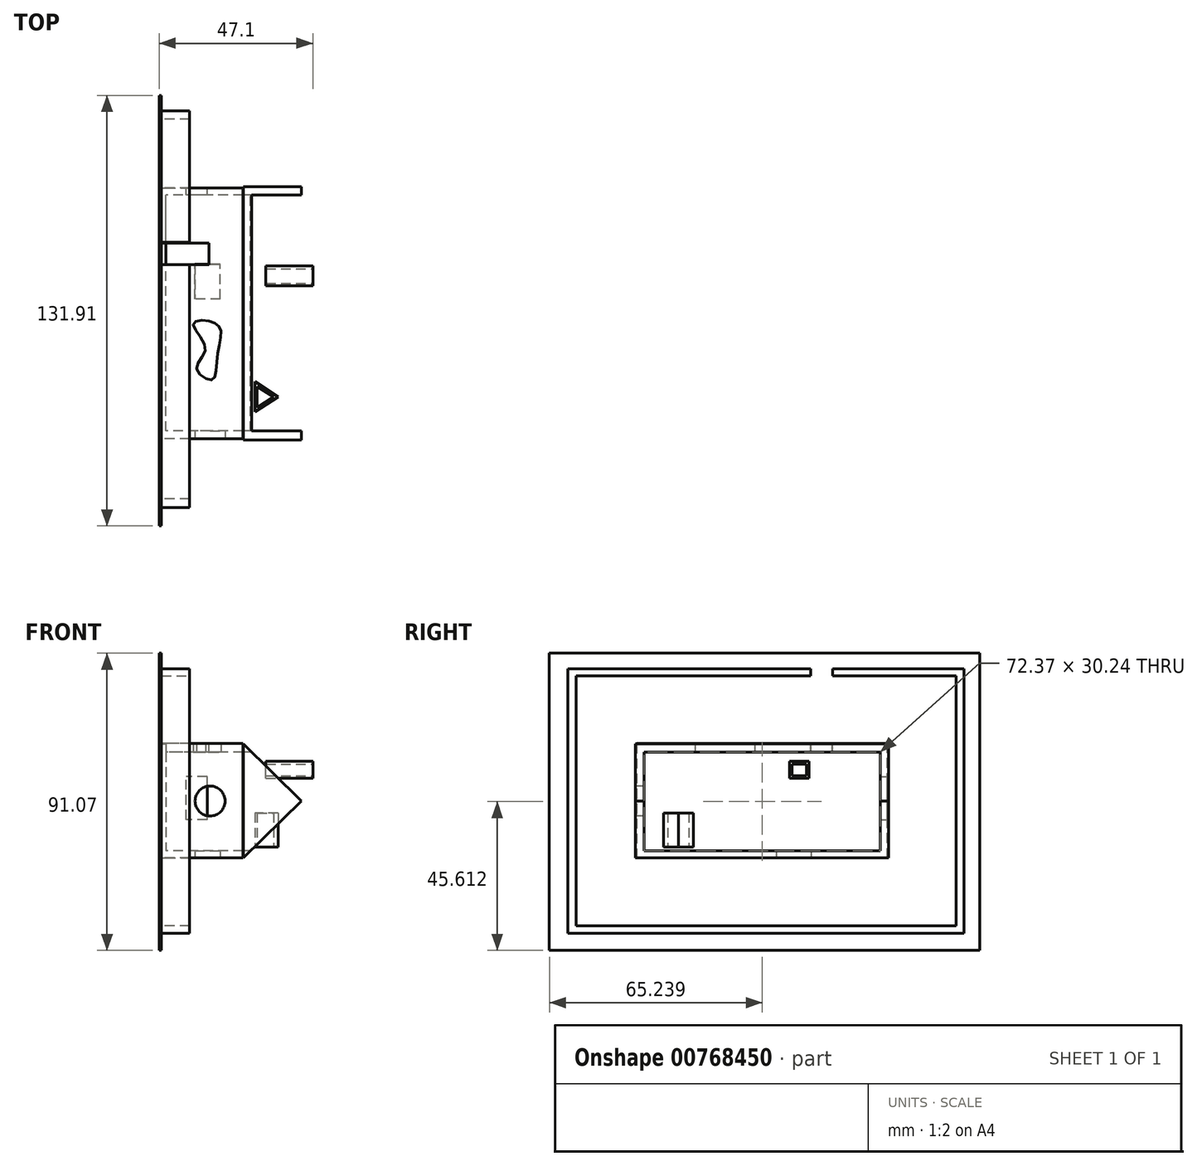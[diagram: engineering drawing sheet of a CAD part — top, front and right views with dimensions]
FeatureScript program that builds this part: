
annotation { "Feature Type Name" : "Feature", "Feature Type Description" : "" }
export const myFeature = defineFeature(function(context is Context, id is Id, definition is map)
    precondition{}
    {
        {
            var Q0;
            Q0=qCreatedBy(makeId("Right.planeOp"),FACE);
            var sketch = newSketch(context, id + "F0", { "sketchPlane" : qUnion([Q0])});
            skLineSegment(sketch, "E0.bottom", {"start": v(-30.7, 35.03) * mm, "end": v(46.12, 35.03) * mm});
            skLineSegment(sketch, "E0.top", {"start": v(-30.7, 0) * mm, "end": v(46.12, 0) * mm});
            skLineSegment(sketch, "E0.left", {"start": v(-30.7, 35.03) * mm, "end": v(-30.7, 0) * mm});
            skLineSegment(sketch, "E0.right", {"start": v(46.12, 35.03) * mm, "end": v(46.12, 0) * mm});
            skSolve(sketch);
        }
        {
            var Q0;
            Q0=makeQuery(id+"F0.imprint","IMPRINT",FACE,{"disambiguationData":[TD([[makeQuery(id+"F0.imprint","IMPRINT",EDGE,{"derivedFrom":sQuery(id+"F0.wireOp",EDGE,"E0.bottom")}),-1.0]])]});
            extrude(context, id + "F1", {"entities" : qUnion([Q0]), "depth" : 25 * mm, "offsetDistance" : 25 * mm});
        }
        {
            var Q0;
            Q0=makeQuery(id+"F1.opExtrude","SWEPT_FACE",FACE,{"disambiguationData":[OSD([sQuery(id+"F0.wireOp",EDGE,"E0.left")])]});
            cPlane(context, id + "F2", {"entities" : qUnion([Q0]), "cplaneType" : CPlaneType.OFFSET, "offset" : 0.4 * mm, "width" : 150 * mm, "height" : 150 * mm});
        }
        {
            var Q0;
            Q0=qCreatedBy(id+"F2.planeOp",FACE);
            var sketch = newSketch(context, id + "F3", { "sketchPlane" : qUnion([Q0])});
            skLineSegment(sketch, "E1", {"start": v(25.09, 0) * mm, "end": v(25.09, 34.92) * mm});
            skLineSegment(sketch, "E2", {"start": v(25.09, 34.92) * mm, "end": v(42.88, 17.46) * mm});
            skLineSegment(sketch, "E3", {"start": v(42.88, 17.46) * mm, "end": v(25.09, 0) * mm});
            skPoint(sketch, "E4", {"position": v(25.09, 17.46) * mm});
            skSolve(sketch);
        }
        {
            var Q0;
            Q0=makeQuery(id+"F3.imprint","IMPRINT",FACE,{"disambiguationData":[TD([[makeQuery(id+"F3.imprint","IMPRINT",EDGE,{"derivedFrom":sQuery(id+"F3.wireOp",EDGE,"E1")}),-1.0]])]});
            extrude(context, id + "F4", {"entities" : qUnion([Q0]), "oppositeDirection" : true, "depth" : 77.6 * mm, "offsetDistance" : 25 * mm});
        }
        {
            var Q0;
            Q0=makeQuery(id+"F1.opExtrude","CAP_FACE",FACE,{"disambiguationData":[OSD([sQuery(id+"F0.wireOp",EDGE,"E0.bottom"),sQuery(id+"F0.wireOp",EDGE,"E0.top"),sQuery(id+"F0.wireOp",EDGE,"E0.left"),sQuery(id+"F0.wireOp",EDGE,"E0.right")])],"isStart":true});
            var sketch = newSketch(context, id + "F5", { "sketchPlane" : qUnion([Q0])});
            skLineSegment(sketch, "E5.bottom", {"start": v(28.4, 32.4) * mm, "end": v(-43.98, 32.4) * mm});
            skLineSegment(sketch, "E5.top", {"start": v(28.4, 2.15) * mm, "end": v(-43.98, 2.15) * mm});
            skLineSegment(sketch, "E5.left", {"start": v(28.4, 32.4) * mm, "end": v(28.4, 2.15) * mm});
            skLineSegment(sketch, "E5.right", {"start": v(-43.98, 32.4) * mm, "end": v(-43.98, 2.15) * mm});
            skLineSegment(sketch, "E6.bottom", {"start": v(-43.98, 12.73) * mm, "end": v(-46.12, 12.73) * mm});
            skLineSegment(sketch, "E6.top", {"start": v(-43.98, 20.43) * mm, "end": v(-46.12, 20.43) * mm});
            skLineSegment(sketch, "E6.left", {"start": v(-43.98, 12.73) * mm, "end": v(-43.98, 20.43) * mm});
            skLineSegment(sketch, "E6.right", {"start": v(-46.12, 12.73) * mm, "end": v(-46.12, 20.43) * mm});
            skSolve(sketch);
        }
        {
            var Q0;
            Q0=makeQuery(id+"F5.imprint","IMPRINT",FACE,{"disambiguationData":[TD([[makeQuery(id+"F5.imprint","IMPRINT",EDGE,{"derivedFrom":sQuery(id+"F5.wireOp",EDGE,"E5.bottom")}),1.0]])]});
            extrude(context, id + "F6", {"entities" : qUnion([Q0]), "operationType" : NewBodyOperationType.REMOVE, "oppositeDirection" : true, "depth" : 113 * mm, "offsetDistance" : 25 * mm});
        }
        {
            var Q0;
            Q0=makeQuery(id+"F1.opExtrude","SWEPT_FACE",FACE,{"disambiguationData":[OSD([sQuery(id+"F0.wireOp",EDGE,"E0.top")])]});
            var sketch = newSketch(context, id + "F7", { "sketchPlane" : qUnion([Q0])});
            skLineSegment(sketch, "E7.bottom", {"start": v(18.02, -12.07) * mm, "end": v(10.18, -12.07) * mm});
            skLineSegment(sketch, "E7.top", {"start": v(18.02, -22.75) * mm, "end": v(10.18, -22.75) * mm});
            skLineSegment(sketch, "E7.left", {"start": v(18.02, -12.07) * mm, "end": v(18.02, -22.75) * mm});
            skLineSegment(sketch, "E7.right", {"start": v(10.18, -12.07) * mm, "end": v(10.18, -22.75) * mm});
            skSolve(sketch);
        }
        {
            var Q0;
            Q0=makeQuery(id+"F7.imprint","IMPRINT",FACE,{"disambiguationData":[TD([[makeQuery(id+"F7.imprint","IMPRINT",EDGE,{"derivedFrom":sQuery(id+"F7.wireOp",EDGE,"E7.bottom")}),1.0]])]});
            extrude(context, id + "F8", {"entities" : qUnion([Q0]), "operationType" : NewBodyOperationType.REMOVE, "oppositeDirection" : true, "depth" : 25 * mm, "offsetDistance" : 25 * mm});
        }
        {
            var Q0;
            Q0=makeQuery(id+"F1.opExtrude","SWEPT_FACE",FACE,{"disambiguationData":[OSD([sQuery(id+"F0.wireOp",EDGE,"E0.bottom")])]});
            var sketch = newSketch(context, id + "F9", { "sketchPlane" : qUnion([Q0])});
            skLineSegment(sketch, "E8.bottom", {"start": v(14.58, 29.22) * mm, "end": v(0, 29.22) * mm});
            skLineSegment(sketch, "E8.top", {"start": v(14.58, 22.6) * mm, "end": v(0, 22.6) * mm});
            skLineSegment(sketch, "E8.left", {"start": v(14.58, 29.22) * mm, "end": v(14.58, 22.6) * mm});
            skLineSegment(sketch, "E8.right", {"start": v(0, 29.22) * mm, "end": v(0, 22.6) * mm});
            skSolve(sketch);
        }
        {
            var Q0;
            Q0=makeQuery(id+"F9.imprint","IMPRINT",FACE,{"disambiguationData":[TD([[makeQuery(id+"F9.imprint","IMPRINT",EDGE,{"derivedFrom":sQuery(id+"F9.wireOp",EDGE,"E8.bottom")}),1.0]])]});
            extrude(context, id + "F10", {"entities" : qUnion([Q0]), "operationType" : NewBodyOperationType.REMOVE, "oppositeDirection" : true, "depth" : 25 * mm, "offsetDistance" : 25 * mm});
        }
        {
            var Q0;
            Q0=makeQuery(id+"F1.opExtrude","SWEPT_FACE",FACE,{"disambiguationData":[OSD([sQuery(id+"F0.wireOp",EDGE,"E0.left")])]});
            var sketch = newSketch(context, id + "F11", { "sketchPlane" : qUnion([Q0])});
            skCircle(sketch, "E9", {"center": v(14.88, 17.43) * mm, "radius": 4.6 * mm});
            skSolve(sketch);
        }
        {
            var Q0;
            Q0=makeQuery(id+"F11.imprint","IMPRINT",FACE,{"disambiguationData":[TD([[makeQuery(id+"F11.imprint","IMPRINT",EDGE,{"derivedFrom":sQuery(id+"F11.wireOp",EDGE,"E9")}),1.0]])]});
            extrude(context, id + "F12", {"entities" : qUnion([Q0]), "operationType" : NewBodyOperationType.REMOVE, "oppositeDirection" : true, "depth" : 25 * mm, "offsetDistance" : 25 * mm});
        }
        {
            var Q0;
            Q0=makeQuery(id+"F1.opExtrude","SWEPT_FACE",FACE,{"disambiguationData":[OSD([sQuery(id+"F0.wireOp",EDGE,"E0.bottom")])]});
            var sketch = newSketch(context, id + "F13", { "sketchPlane" : qUnion([Q0])});
            skFitSpline(sketch, "E10", {"points": [v(14.56, 5.34) * mm, v(18.11, 2.68) * mm, v(17.03, -6.13) * mm, v(15.45, -12.74) * mm, v(10.78, -9.13) * mm, v(13.5, -3.04) * mm, v(9.73, 4.4) * mm, v(14.56, 5.34) * mm]});
            skSolve(sketch);
        }
        {
            var Q0;
            Q0=makeQuery(id+"F13.imprint","IMPRINT",FACE,{"disambiguationData":[TD([[makeQuery(id+"F13.imprint","IMPRINT",EDGE,{"derivedFrom":sQuery(id+"F13.wireOp",EDGE,"E10")}),-1.0]])]});
            extrude(context, id + "F14", {"entities" : qUnion([Q0]), "operationType" : NewBodyOperationType.REMOVE, "oppositeDirection" : true, "depth" : 25 * mm, "offsetDistance" : 25 * mm});
        }
        {
            var Q0;
            Q0=qCreatedBy(makeId("Right.planeOp"),FACE);
            cPlane(context, id + "F15", {"entities" : qUnion([Q0]), "cplaneType" : CPlaneType.OFFSET, "offset" : 46.4 * mm, "width" : 150 * mm, "height" : 150 * mm});
        }
        {
            var Q0;
            Q0=qCreatedBy(id+"F15.planeOp",FACE);
            var sketch = newSketch(context, id + "F16", { "sketchPlane" : qUnion([Q0])});
            skLineSegment(sketch, "E11.bottom", {"start": v(22.16, 24.47) * mm, "end": v(16.16, 24.47) * mm});
            skLineSegment(sketch, "E11.top", {"start": v(22.16, 29.6) * mm, "end": v(16.16, 29.6) * mm});
            skLineSegment(sketch, "E11.left", {"start": v(22.16, 24.47) * mm, "end": v(22.16, 29.6) * mm});
            skLineSegment(sketch, "E11.right", {"start": v(16.16, 24.47) * mm, "end": v(16.16, 29.6) * mm});
            skSolve(sketch);
        }
        {
            var Q0;
            Q0=makeQuery(id+"F16.imprint","IMPRINT",FACE,{"disambiguationData":[TD([[makeQuery(id+"F16.imprint","IMPRINT",EDGE,{"derivedFrom":sQuery(id+"F16.wireOp",EDGE,"E11.bottom")}),-1.0]])]});
            extrude(context, id + "F17", {"entities" : qUnion([Q0]), "operationType" : NewBodyOperationType.ADD, "oppositeDirection" : true, "depth" : 14.4 * mm, "offsetDistance" : 25 * mm});
        }
        {
            var Q0;
            Q0=makeQuery(id+"F17.opExtrude","CAP_FACE",FACE,{"disambiguationData":[OSD([sQuery(id+"F16.wireOp",EDGE,"E11.bottom"),sQuery(id+"F16.wireOp",EDGE,"E11.top"),sQuery(id+"F16.wireOp",EDGE,"E11.left"),sQuery(id+"F16.wireOp",EDGE,"E11.right")])],"isStart":true});
            var sketch = newSketch(context, id + "F18", { "sketchPlane" : qUnion([Q0])});
            skLineSegment(sketch, "E12.bottom", {"start": v(21.35, 25.23) * mm, "end": v(16.92, 25.23) * mm});
            skLineSegment(sketch, "E12.top", {"start": v(21.35, 28.75) * mm, "end": v(16.92, 28.75) * mm});
            skLineSegment(sketch, "E12.left", {"start": v(21.35, 25.23) * mm, "end": v(21.35, 28.75) * mm});
            skLineSegment(sketch, "E12.right", {"start": v(16.92, 25.23) * mm, "end": v(16.92, 28.75) * mm});
            skSolve(sketch);
        }
        {
            var Q0;
            Q0=makeQuery(id+"F18.imprint","IMPRINT",FACE,{"disambiguationData":[TD([[makeQuery(id+"F18.imprint","IMPRINT",EDGE,{"derivedFrom":sQuery(id+"F18.wireOp",EDGE,"E12.bottom")}),-1.0]])]});
            extrude(context, id + "F19", {"entities" : qUnion([Q0]), "operationType" : NewBodyOperationType.REMOVE, "oppositeDirection" : true, "depth" : 25 * mm, "offsetDistance" : 25 * mm});
        }
        {
            var Q0;
            Q0=qCreatedBy(makeId("Right.planeOp"),FACE);
            var sketch = newSketch(context, id + "F20", { "sketchPlane" : qUnion([Q0])});
            skLineSegment(sketch, "E13.bottom", {"start": v(-30.64, 34.9) * mm, "end": v(46.1, 34.9) * mm});
            skLineSegment(sketch, "E13.top", {"start": v(-30.64, 0) * mm, "end": v(46.1, 0) * mm});
            skLineSegment(sketch, "E13.left", {"start": v(-30.64, 34.9) * mm, "end": v(-30.64, 0) * mm});
            skLineSegment(sketch, "E13.right", {"start": v(46.1, 34.9) * mm, "end": v(46.1, 0) * mm});
            skSolve(sketch);
        }
        {
            var Q0;
            Q0=makeQuery(id+"F20.imprint","IMPRINT",FACE,{"disambiguationData":[TD([[makeQuery(id+"F20.imprint","IMPRINT",EDGE,{"derivedFrom":sQuery(id+"F20.wireOp",EDGE,"E13.bottom")}),-1.0]])]});
            extrude(context, id + "F21", {"entities" : qUnion([Q0]), "operationType" : NewBodyOperationType.ADD, "depth" : 1.3 * mm, "offsetDistance" : 25 * mm});
        }
        {
            var Q0;
            Q0=qCreatedBy(makeId("Right.planeOp"),FACE);
            var sketch = newSketch(context, id + "F22", { "sketchPlane" : qUnion([Q0])});
            skLineSegment(sketch, "E14.bottom", {"start": v(74.46, -28.34) * mm, "end": v(-57.45, -28.34) * mm});
            skLineSegment(sketch, "E14.top", {"start": v(74.46, 62.73) * mm, "end": v(-57.45, 62.73) * mm});
            skLineSegment(sketch, "E14.left", {"start": v(74.46, -28.34) * mm, "end": v(74.46, 62.73) * mm});
            skLineSegment(sketch, "E14.right", {"start": v(-57.45, -28.34) * mm, "end": v(-57.45, 62.73) * mm});
            skSolve(sketch);
        }
        {
            var Q0;
            Q0=makeQuery(id+"F22.imprint","IMPRINT",FACE,{"disambiguationData":[TD([[makeQuery(id+"F22.imprint","IMPRINT",EDGE,{"derivedFrom":sQuery(id+"F22.wireOp",EDGE,"E14.bottom")}),-1.0]])]});
            extrude(context, id + "F23", {"entities" : qUnion([Q0]), "operationType" : NewBodyOperationType.ADD, "oppositeDirection" : true, "depth" : 0.7 * mm, "offsetDistance" : 25 * mm});
        }
        {
            var Q0;
            Q0=makeQuery(id+"F23.opExtrude","CAP_FACE",FACE,{"disambiguationData":[OSD([sQuery(id+"F22.wireOp",EDGE,"E14.bottom"),sQuery(id+"F22.wireOp",EDGE,"E14.top"),sQuery(id+"F22.wireOp",EDGE,"E14.left"),sQuery(id+"F22.wireOp",EDGE,"E14.right")])],"isStart":true});
            var sketch = newSketch(context, id + "F24", { "sketchPlane" : qUnion([Q0])});
            skLineSegment(sketch, "E15.bottom", {"start": v(69.66, -23.1) * mm, "end": v(-51.83, -23.1) * mm});
            skLineSegment(sketch, "E15.top", {"start": v(69.66, 57.9) * mm, "end": v(-51.83, 57.9) * mm});
            skLineSegment(sketch, "E15.left", {"start": v(69.66, -23.1) * mm, "end": v(69.66, 57.9) * mm});
            skLineSegment(sketch, "E15.right", {"start": v(-51.83, -23.1) * mm, "end": v(-51.83, 57.9) * mm});
            skLineSegment(sketch, "E16.bottom", {"start": v(67.18, -20.76) * mm, "end": v(-49.22, -20.76) * mm});
            skLineSegment(sketch, "E16.top", {"start": v(67.18, 55.83) * mm, "end": v(-49.22, 55.83) * mm});
            skLineSegment(sketch, "E16.left", {"start": v(67.18, -20.76) * mm, "end": v(67.18, 55.83) * mm});
            skLineSegment(sketch, "E16.right", {"start": v(-49.22, -20.76) * mm, "end": v(-49.22, 55.83) * mm});
            skSolve(sketch);
        }
        {
            var Q0;
            Q0=makeQuery(id+"F24.imprint","IMPRINT",FACE,{"disambiguationData":[TD([[makeQuery(id+"F24.imprint","IMPRINT",EDGE,{"derivedFrom":sQuery(id+"F24.wireOp",EDGE,"E15.bottom")}),-1.0]])]});
            extrude(context, id + "F25", {"entities" : qUnion([Q0]), "operationType" : NewBodyOperationType.ADD, "depth" : 8.6 * mm, "offsetDistance" : 25 * mm});
        }
        {
            var Q0;
            Q0=makeQuery(id+"F25.opExtrude","SWEPT_FACE",FACE,{"disambiguationData":[OSD([sQuery(id+"F24.wireOp",EDGE,"E15.top")])]});
            var sketch = newSketch(context, id + "F26", { "sketchPlane" : qUnion([Q0])});
            skLineSegment(sketch, "E17.bottom", {"start": v(8.6, 29.4) * mm, "end": v(0, 29.4) * mm});
            skLineSegment(sketch, "E17.top", {"start": v(8.6, 22.59) * mm, "end": v(0, 22.59) * mm});
            skLineSegment(sketch, "E17.left", {"start": v(8.6, 29.4) * mm, "end": v(8.6, 22.59) * mm});
            skLineSegment(sketch, "E17.right", {"start": v(0, 29.4) * mm, "end": v(0, 22.59) * mm});
            skSolve(sketch);
        }
        {
            var Q0;
            Q0=makeQuery(id+"F26.imprint","IMPRINT",FACE,{"disambiguationData":[TD([[makeQuery(id+"F26.imprint","IMPRINT",EDGE,{"derivedFrom":sQuery(id+"F26.wireOp",EDGE,"E17.bottom")}),1.0]])]});
            extrude(context, id + "F27", {"entities" : qUnion([Q0]), "operationType" : NewBodyOperationType.REMOVE, "oppositeDirection" : true, "depth" : 9.3 * mm, "offsetDistance" : 25 * mm});
        }
        {
            var Q0;
            Q0=qCreatedBy(makeId("Top.planeOp"),FACE);
            cPlane(context, id + "F28", {"entities" : qUnion([Q0]), "cplaneType" : CPlaneType.OFFSET, "offset" : 3.3 * mm, "width" : 150 * mm, "height" : 150 * mm});
        }
        {
            var Q0;
            Q0=qCreatedBy(id+"F28.planeOp",FACE);
            var sketch = newSketch(context, id + "F29", { "sketchPlane" : qUnion([Q0])});
            skLineSegment(sketch, "E18", {"start": v(35.76, -17.94) * mm, "end": v(28.61, -22.5) * mm});
            skLineSegment(sketch, "E19", {"start": v(28.61, -22.5) * mm, "end": v(28.61, -13.28) * mm});
            skLineSegment(sketch, "E20", {"start": v(28.61, -13.28) * mm, "end": v(35.76, -17.94) * mm});
            skSolve(sketch);
        }
        {
            var Q0;
            Q0=makeQuery(id+"F29.imprint","IMPRINT",FACE,{"disambiguationData":[TD([[makeQuery(id+"F29.imprint","IMPRINT",EDGE,{"derivedFrom":sQuery(id+"F29.wireOp",EDGE,"E18")}),-1.0]])]});
            extrude(context, id + "F30", {"entities" : qUnion([Q0]), "operationType" : NewBodyOperationType.ADD, "depth" : 10.5 * mm, "offsetDistance" : 25 * mm});
        }
        {
            var Q0;
            Q0=makeQuery(id+"F30.opExtrude","CAP_FACE",FACE,{"disambiguationData":[OSD([sQuery(id+"F29.wireOp",EDGE,"E18"),sQuery(id+"F29.wireOp",EDGE,"E19"),sQuery(id+"F29.wireOp",EDGE,"E20")])],"isStart":true});
            var sketch = newSketch(context, id + "F31", { "sketchPlane" : qUnion([Q0])});
            skLineSegment(sketch, "E21", {"start": v(29.29, 21.22) * mm, "end": v(29.29, 14.71) * mm});
            skLineSegment(sketch, "E22", {"start": v(29.29, 14.71) * mm, "end": v(34.4, 17.94) * mm});
            skLineSegment(sketch, "E23", {"start": v(34.4, 17.94) * mm, "end": v(29.29, 21.22) * mm});
            skSolve(sketch);
        }
        {
            var Q0;
            Q0=makeQuery(id+"F31.imprint","IMPRINT",FACE,{"disambiguationData":[TD([[makeQuery(id+"F31.imprint","IMPRINT",EDGE,{"derivedFrom":sQuery(id+"F31.wireOp",EDGE,"E21")}),1.0]])]});
            extrude(context, id + "F32", {"entities" : qUnion([Q0]), "operationType" : NewBodyOperationType.REMOVE, "oppositeDirection" : true, "depth" : 12.65 * mm, "offsetDistance" : 25 * mm});
        }
        {
            var Q0;
            Q0=makeQuery(id+"F1.opExtrude","SWEPT_FACE",FACE,{"disambiguationData":[OSD([sQuery(id+"F0.wireOp",EDGE,"E0.right")])]});
            var sketch = newSketch(context, id + "F33", { "sketchPlane" : qUnion([Q0])});
            skLineSegment(sketch, "E24.bottom", {"start": v(-14, 11.74) * mm, "end": v(-7.5, 11.74) * mm});
            skLineSegment(sketch, "E24.top", {"start": v(-14, 24.96) * mm, "end": v(-7.5, 24.96) * mm});
            skLineSegment(sketch, "E24.left", {"start": v(-14, 11.74) * mm, "end": v(-14, 24.96) * mm});
            skLineSegment(sketch, "E24.right", {"start": v(-7.5, 11.74) * mm, "end": v(-7.5, 24.96) * mm});
            skSolve(sketch);
        }
        {
            var Q0;
            Q0=makeQuery(id+"F33.imprint","IMPRINT",FACE,{"disambiguationData":[TD([[makeQuery(id+"F33.imprint","IMPRINT",EDGE,{"derivedFrom":sQuery(id+"F33.wireOp",EDGE,"E24.bottom")}),1.0]])]});
            extrude(context, id + "F34", {"entities" : qUnion([Q0]), "operationType" : NewBodyOperationType.REMOVE, "oppositeDirection" : true, "depth" : 25 * mm, "offsetDistance" : 25 * mm});
        }
    });
